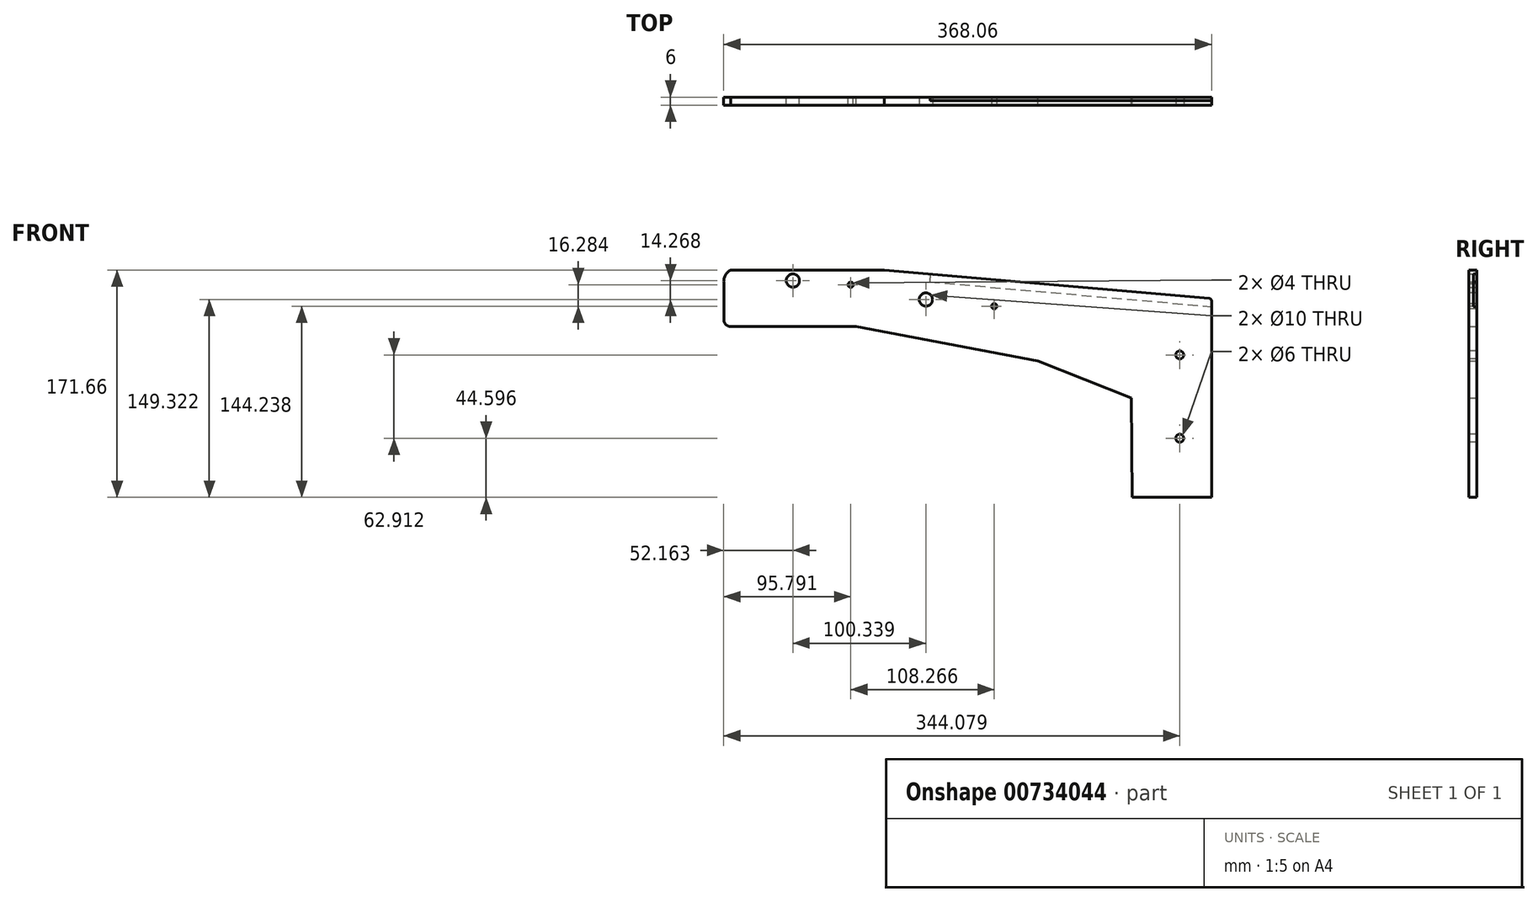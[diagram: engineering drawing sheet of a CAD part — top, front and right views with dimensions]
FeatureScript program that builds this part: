
annotation { "Feature Type Name" : "Feature", "Feature Type Description" : "" }
export const myFeature = defineFeature(function(context is Context, id is Id, definition is map)
    precondition{}
    {
        {
            var Q0;
            Q0=qCreatedBy(makeId("Front.planeOp"),FACE);
            var sketch = newSketch(context, id + "F0", { "sketchPlane" : qUnion([Q0])});
            skArc(sketch, "E0", {"start": v(-54.77, 8.07) * mm, "mid": v(-58.95, 3.73) * mm, "end": v(-59.88, -2.22) * mm});
            skLineSegment(sketch, "E1", {"start": v(-38.64, -34.67) * mm, "end": v(39.88, -34.67) * mm});
            skLineSegment(sketch, "E2", {"start": v(308.06, -13.59) * mm, "end": v(308.06, -163.59) * mm});
            skLineSegment(sketch, "E3", {"start": v(308.06, -163.59) * mm, "end": v(248.06, -163.59) * mm});
            skLineSegment(sketch, "E4", {"start": v(-59.88, -2.22) * mm, "end": v(-59.88, -29.67) * mm});
            skLineSegment(sketch, "E5", {"start": v(-54.88, -34.67) * mm, "end": v(-38.64, -34.67) * mm});
            skPoint(sketch, "E6.visualSharp", {"position": v(-59.88, -34.67) * mm});
            skArc(sketch, "E6.filletArc", {"start": v(-59.88, -29.67) * mm, "mid": v(-58.42, -33.2) * mm, "end": v(-54.88, -34.67) * mm});
            skPoint(sketch, "E7", {"position": v(35.8, -3.07) * mm});
            skCircle(sketch, "E8", {"center": v(35.8, -3.07) * mm, "radius": 2 * mm});
            skLineSegment(sketch, "E9", {"start": v(248.06, -163.59) * mm, "end": v(247.38, -88.6) * mm});
            skLineSegment(sketch, "E10", {"start": v(177.12, -60.52) * mm, "end": v(247.38, -88.6) * mm});
            skLineSegment(sketch, "E11", {"start": v(39.88, -34.67) * mm, "end": v(177.12, -60.52) * mm});
            skLineSegment(sketch, "E12", {"start": v(308.06, -13.59) * mm, "end": v(61.1, 8.07) * mm});
            skLineSegment(sketch, "E13", {"start": v(61.1, 8.07) * mm, "end": v(-54.77, 8.07) * mm});
            skSolve(sketch);
        }
        {
            var Q0;
            Q0=qSketchRegion(id+"F0",true);
            extrude(context, id + "F1", {"entities" : qUnion([Q0]), "depth" : 6 * mm, "offsetDistance" : 25 * mm});
        }
        {
            var Q0;
            Q0=makeQuery(id+"F1.opExtrude","CAP_FACE",FACE,{"disambiguationData":[OSD([sQuery(id+"F0.wireOp",EDGE,"69VMhtjD-FHem-1Nzl-ZIln-yZqZocFnkeLI"),sQuery(id+"F0.wireOp",EDGE,"E0"),sQuery(id+"F0.wireOp",EDGE,"E1"),sQuery(id+"F0.wireOp",EDGE,"E2"),sQuery(id+"F0.wireOp",EDGE,"E3"),sQuery(id+"F0.wireOp",EDGE,"zyuM4KxI-rK7D-eBj5-RQWG-Z7kNhVQKbpSr"),sQuery(id+"F0.wireOp",EDGE,"E4"),sQuery(id+"F0.wireOp",EDGE,"E5"),sQuery(id+"F0.wireOp",EDGE,"E6.filletArc"),sQuery(id+"F0.wireOp",EDGE,"Sq1smuhl-J9rg-3BfP-JIUe-rn6nJ9PzM2vD"),sQuery(id+"F0.wireOp",EDGE,"PUNmVgVp-qFH2-CwZl-KZ4H-ZFihZqVa5LSU"),sQuery(id+"F0.wireOp",EDGE,"RsVNkQyW-0Ggk-FljP-8XP7-kQ1KxApps7TM")])],"isStart":false});
            var sketch = newSketch(context, id + "F2", { "sketchPlane" : qUnion([Q0])});
            skLineSegment(sketch, "E14", {"start": v(-49.88, 0) * mm, "end": v(-59.97, 0) * mm});
            skLineSegment(sketch, "E15", {"start": v(-49.88, 0) * mm, "end": v(30.12, 0) * mm});
            skLineSegment(sketch, "E16", {"start": v(30.12, 0) * mm, "end": v(92.5, -8.77) * mm});
            skLineSegment(sketch, "E17", {"start": v(92.5, -8.77) * mm, "end": v(92.5, -14.27) * mm});
            skCircle(sketch, "E18", {"center": v(92.5, -14.27) * mm, "radius": 5 * mm});
            skSolve(sketch);
        }
        {
            var Q0;
            Q0=qSketchRegion(id+"F2",true);
            extrude(context, id + "F3", {"entities" : qUnion([Q0]), "operationType" : NewBodyOperationType.REMOVE, "endBound" : BoundingType.THROUGH_ALL, "oppositeDirection" : true, "depth" : 25 * mm, "offsetDistance" : 25 * mm});
        }
        {
            var Q0;
            Q0=makeQuery(id+"F1.opExtrude","CAP_FACE",FACE,{"disambiguationData":[OSD([sQuery(id+"F0.wireOp",EDGE,"69VMhtjD-FHem-1Nzl-ZIln-yZqZocFnkeLI"),sQuery(id+"F0.wireOp",EDGE,"E0"),sQuery(id+"F0.wireOp",EDGE,"E1"),sQuery(id+"F0.wireOp",EDGE,"E2"),sQuery(id+"F0.wireOp",EDGE,"E3"),sQuery(id+"F0.wireOp",EDGE,"zyuM4KxI-rK7D-eBj5-RQWG-Z7kNhVQKbpSr"),sQuery(id+"F0.wireOp",EDGE,"E4"),sQuery(id+"F0.wireOp",EDGE,"E5"),sQuery(id+"F0.wireOp",EDGE,"E6.filletArc"),sQuery(id+"F0.wireOp",EDGE,"Sq1smuhl-J9rg-3BfP-JIUe-rn6nJ9PzM2vD"),sQuery(id+"F0.wireOp",EDGE,"PUNmVgVp-qFH2-CwZl-KZ4H-ZFihZqVa5LSU"),sQuery(id+"F0.wireOp",EDGE,"RsVNkQyW-0Ggk-FljP-8XP7-kQ1KxApps7TM")])],"isStart":false});
            var sketch = newSketch(context, id + "F4", { "sketchPlane" : qUnion([Q0])});
            skLineSegment(sketch, "E19", {"start": v(111.32, -0.3) * mm, "end": v(111.32, -12.3) * mm});
            skCircle(sketch, "E20", {"center": v(284.08, -119) * mm, "radius": 3 * mm});
            skCircle(sketch, "E21", {"center": v(284.08, -56.08) * mm, "radius": 3 * mm});
            skLineSegment(sketch, "E22", {"start": v(284.08, -56.08) * mm, "end": v(284.08, -119) * mm});
            skSolve(sketch);
        }
        {
            var Q0;
            Q0=qSketchRegion(id+"F4",true);
            extrude(context, id + "F5", {"entities" : qUnion([Q0]), "operationType" : NewBodyOperationType.REMOVE, "endBound" : BoundingType.THROUGH_ALL, "oppositeDirection" : true, "depth" : 25 * mm, "offsetDistance" : 25 * mm});
        }
        {
            var Q0;
            Q0=makeQuery(id+"F1.opExtrude","CAP_FACE",FACE,{"disambiguationData":[OSD([sQuery(id+"F0.wireOp",EDGE,"69VMhtjD-FHem-1Nzl-ZIln-yZqZocFnkeLI"),sQuery(id+"F0.wireOp",EDGE,"E0"),sQuery(id+"F0.wireOp",EDGE,"E1"),sQuery(id+"F0.wireOp",EDGE,"E2"),sQuery(id+"F0.wireOp",EDGE,"E3"),sQuery(id+"F0.wireOp",EDGE,"zyuM4KxI-rK7D-eBj5-RQWG-Z7kNhVQKbpSr"),sQuery(id+"F0.wireOp",EDGE,"E4"),sQuery(id+"F0.wireOp",EDGE,"E5"),sQuery(id+"F0.wireOp",EDGE,"E6.filletArc"),sQuery(id+"F0.wireOp",EDGE,"Sq1smuhl-J9rg-3BfP-JIUe-rn6nJ9PzM2vD"),sQuery(id+"F0.wireOp",EDGE,"PUNmVgVp-qFH2-CwZl-KZ4H-ZFihZqVa5LSU"),sQuery(id+"F0.wireOp",EDGE,"RsVNkQyW-0Ggk-FljP-8XP7-kQ1KxApps7TM")])],"isStart":true});
            var sketch = newSketch(context, id + "F6", { "sketchPlane" : qUnion([Q0])});
            skCircle(sketch, "E23", {"center": v(7.84, 0) * mm, "radius": 5 * mm});
            skSolve(sketch);
        }
        {
            var Q0;
            Q0=qSketchRegion(id+"F6",true);
            extrude(context, id + "F7", {"entities" : qUnion([Q0]), "operationType" : NewBodyOperationType.REMOVE, "endBound" : BoundingType.THROUGH_ALL, "oppositeDirection" : true, "depth" : 25 * mm, "offsetDistance" : 25 * mm});
        }
        {
            var Q0;
            Q0=qSketchRegion(id+"F0",true);
            extrude(context, id + "F8", {"entities" : qUnion([Q0]), "operationType" : NewBodyOperationType.REMOVE, "endBound" : BoundingType.THROUGH_ALL, "oppositeDirection" : true, "depth" : 25 * mm, "offsetDistance" : 25 * mm});
        }
        {
            var Q0;
            Q0=makeQuery(id+"F1.opExtrude","CAP_FACE",FACE,{"disambiguationData":[OSD([sQuery(id+"F0.wireOp",EDGE,"69VMhtjD-FHem-1Nzl-ZIln-yZqZocFnkeLI"),sQuery(id+"F0.wireOp",EDGE,"E0"),sQuery(id+"F0.wireOp",EDGE,"E1"),sQuery(id+"F0.wireOp",EDGE,"E2"),sQuery(id+"F0.wireOp",EDGE,"E3"),sQuery(id+"F0.wireOp",EDGE,"zyuM4KxI-rK7D-eBj5-RQWG-Z7kNhVQKbpSr"),sQuery(id+"F0.wireOp",EDGE,"E4"),sQuery(id+"F0.wireOp",EDGE,"E5"),sQuery(id+"F0.wireOp",EDGE,"E6.filletArc"),sQuery(id+"F0.wireOp",EDGE,"Sq1smuhl-J9rg-3BfP-JIUe-rn6nJ9PzM2vD"),sQuery(id+"F0.wireOp",EDGE,"PUNmVgVp-qFH2-CwZl-KZ4H-ZFihZqVa5LSU"),sQuery(id+"F0.wireOp",EDGE,"RsVNkQyW-0Ggk-FljP-8XP7-kQ1KxApps7TM"),sQuery(id+"F0.wireOp",EDGE,"E8")])],"isStart":false});
            var sketch = newSketch(context, id + "F9", { "sketchPlane" : qUnion([Q0])});
            skPoint(sketch, "E24", {"position": v(144.06, -19.35) * mm});
            skCircle(sketch, "E25", {"center": v(144.06, -19.35) * mm, "radius": 2 * mm});
            skSolve(sketch);
        }
        {
            var Q0;
            Q0=qSketchRegion(id+"F9",true);
            extrude(context, id + "F10", {"entities" : qUnion([Q0]), "operationType" : NewBodyOperationType.REMOVE, "endBound" : BoundingType.THROUGH_ALL, "oppositeDirection" : true, "depth" : 25 * mm, "offsetDistance" : 25 * mm});
        }
        {
            var Q0;
            Q0=makeQuery(id+"F1.opExtrude","CAP_FACE",FACE,{"disambiguationData":[OSD([sQuery(id+"F0.wireOp",EDGE,"E0"),sQuery(id+"F0.wireOp",EDGE,"E1"),sQuery(id+"F0.wireOp",EDGE,"E2"),sQuery(id+"F0.wireOp",EDGE,"E3"),sQuery(id+"F0.wireOp",EDGE,"E4"),sQuery(id+"F0.wireOp",EDGE,"E5"),sQuery(id+"F0.wireOp",EDGE,"E6.filletArc"),sQuery(id+"F0.wireOp",EDGE,"E8"),sQuery(id+"F0.wireOp",EDGE,"E9"),sQuery(id+"F0.wireOp",EDGE,"E10"),sQuery(id+"F0.wireOp",EDGE,"E11"),sQuery(id+"F0.wireOp",EDGE,"E12"),sQuery(id+"F0.wireOp",EDGE,"E13")])],"isStart":true});
            var sketch = newSketch(context, id + "F11", { "sketchPlane" : qUnion([Q0])});
            skPoint(sketch, "E26.start.orphan", {"position": v(-95.9, 5.01) * mm});
            skLineSegment(sketch, "E27", {"start": v(-95.9, 5.01) * mm, "end": v(-298.13, -12.71) * mm});
            skLineSegment(sketch, "E28", {"start": v(-95.38, -0.96) * mm, "end": v(-297.6, -18.7) * mm});
            skLineSegment(sketch, "E29", {"start": v(-95.9, 5.01) * mm, "end": v(-95.38, -0.96) * mm});
            skLineSegment(sketch, "E30", {"start": v(-298.13, -12.71) * mm, "end": v(-308.06, -13.59) * mm});
            skLineSegment(sketch, "E31", {"start": v(-297.6, -18.7) * mm, "end": v(-308.06, -19.6) * mm});
            skLineSegment(sketch, "E32", {"start": v(-308.06, -19.6) * mm, "end": v(-308.06, -13.59) * mm});
            skSolve(sketch);
        }
        {
            var Q0;
            Q0=qSketchRegion(id+"F11",true);
            extrude(context, id + "F12", {"entities" : qUnion([Q0]), "operationType" : NewBodyOperationType.REMOVE, "oppositeDirection" : true, "depth" : 2.5 * mm, "offsetDistance" : 25 * mm});
        }
        {
            var Q0;
            Q0=makeQuery(id+"F1.opExtrude","SWEPT_EDGE",EDGE,{"disambiguationData":[OSD([sQuery(id+"F0.wireOp",EDGE,"E2"),sQuery(id+"F0.wireOp",EDGE,"E12")])]});
            fillet(context, id + "F13", {"entities" : qUnion([Q0]), "radius" : 2 * mm, "tangentPropagation" : true, "allowEdgeOverflow" : false});
        }
    });
